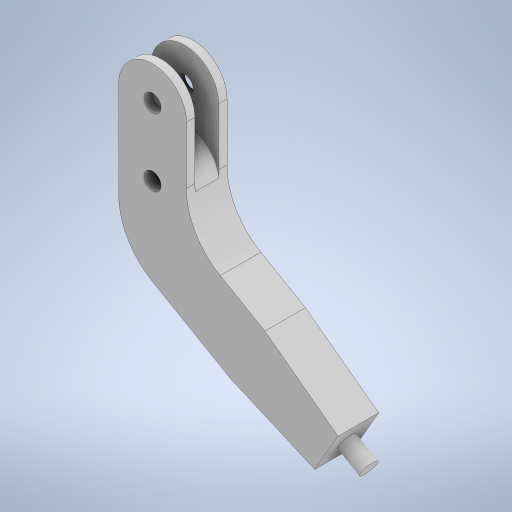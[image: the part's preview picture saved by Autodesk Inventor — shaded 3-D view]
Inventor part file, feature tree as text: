
AUTODESK INVENTOR PART (.ipt)
format: ipt  version: 2024.3 (Build 283343000, 343)  size: 354,304 bytes
history: native  units: mm
features: extrude x5, sketch x5, fillet x3, other x1
ambient origin geometry x8: Origin, YZ Plane, XZ Plane, XY Plane, X Axis, Y Axis, Z Axis, Center Point
bodies: Body1 (feature_tree)
feature tree (14):
  other  "ソリッド1"
  extrude  "押し出し1"  Depth=40.0mm
  extrude  "押し出し4"  Depth=318.0mm
  extrude  "押し出し5"  Depth=24.0mm TaperAngle=0.0deg
  fillet  "フィレット1"  Radius=10.0mm
  fillet  "フィレット2"  Radius=20.0mm
  extrude  "押し出し6"  Depth=2.459mm
  extrude  "押し出し7"  Depth=2.459mm
  fillet  "フィレット4"  Radius=10.0mm
  sketch  "スケッチ1"
  sketch  "スケッチ6"
  sketch  "スケッチ8"
  sketch  "スケッチ9"
  sketch  "スケッチ11"
